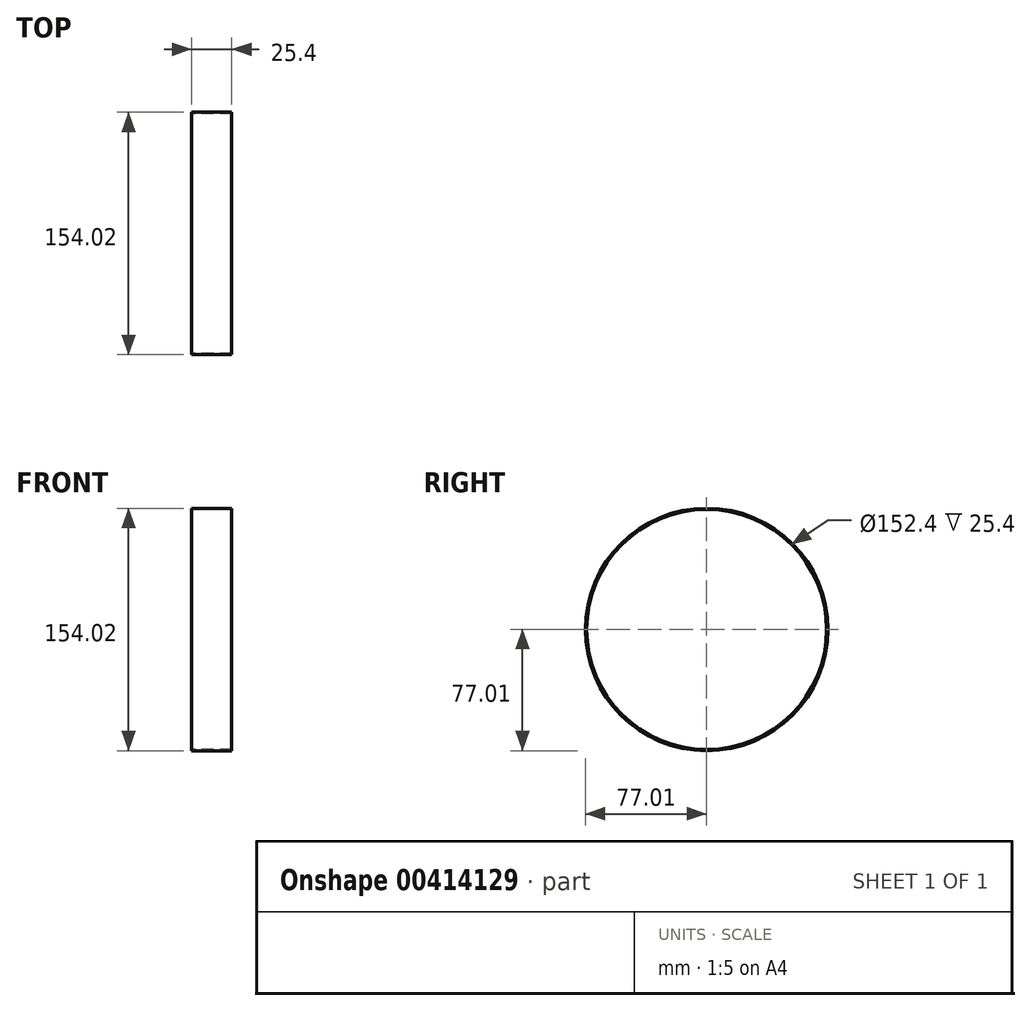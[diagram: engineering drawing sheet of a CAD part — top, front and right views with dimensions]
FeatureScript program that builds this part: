
annotation { "Feature Type Name" : "Feature", "Feature Type Description" : "" }
export const myFeature = defineFeature(function(context is Context, id is Id, definition is map)
    precondition{}
    {
        {
            var Q0;
            Q0=qCreatedBy(makeId("Front.planeOp"),FACE);
            var sketch = newSketch(context, id + "F0", { "sketchPlane" : qUnion([Q0])});
            skLineSegment(sketch, "E0", {"start": v(-59.72, 0) * mm, "end": v(56.3, 0) * mm, "construction": true});
            skLineSegment(sketch, "E1", {"start": v(0, 76.2) * mm, "end": v(0, 77.01) * mm});
            skLineSegment(sketch, "E2", {"start": v(0, 77.01) * mm, "end": v(25.4, 77.01) * mm});
            skLineSegment(sketch, "E3", {"start": v(25.4, 0) * mm, "end": v(19.05, 0) * mm});
            skLineSegment(sketch, "E4", {"start": v(25.4, 76.2) * mm, "end": v(0, 76.2) * mm});
            skLineSegment(sketch, "E5", {"start": v(25.4, 77.01) * mm, "end": v(25.4, 76.2) * mm});
            skSolve(sketch);
        }
        {
            var Q0;
            Q0 = qSketchRegion(id + "F0", true);
            var Q1;
            Q1=sQuery(id+"F0.wireOp",EDGE,"E0");
            revolve(context, id + "F1", {"entities" : qUnion([Q0]), "axis" : qUnion([Q1]), "revolveType" : RevolveType.FULL});
        }
    });
